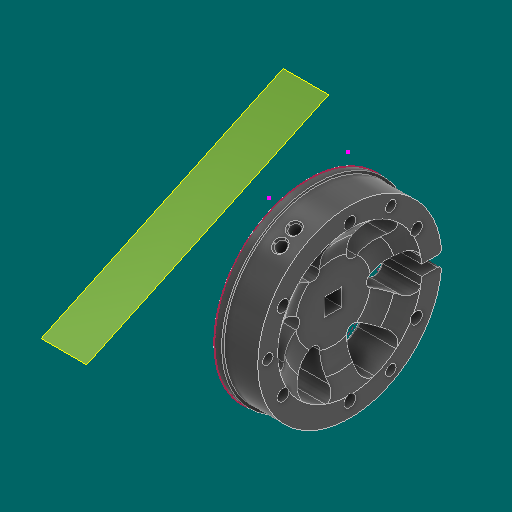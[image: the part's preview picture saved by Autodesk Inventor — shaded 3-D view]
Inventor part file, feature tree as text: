
AUTODESK INVENTOR PART (.ipt)
format: ipt  version: 2023.1 (Build 271208000, 208)  size: 540,672 bytes
history: native  units: in
note: dims shown in document units (in); Inventor stores cm internally (conversion verified against a paired STEP export)
features: sketch x7, other x4, plane x1
ambient origin geometry x8: Origin, YZ Plane, XZ Plane, XY Plane, X Axis, Y Axis, Z Axis, Center Point
bodies: Solid1 (feature_tree)
feature tree (12):
  other  "WheelHalf.ipt"
  other  "Solid1::WheelHalf.ipt"
  other  "TaggingFeature1"
  sketch  "Sketch1"  dims[d0=0.3937in]
  sketch  "Sketch2"
  sketch  "Sketch3"
  sketch  "Sketch4"
  sketch  "Sketch5"
  sketch  "Sketch6"
  sketch  "Sketch7"
  plane  "Work Plane1"
  other  "Work Axis1"
